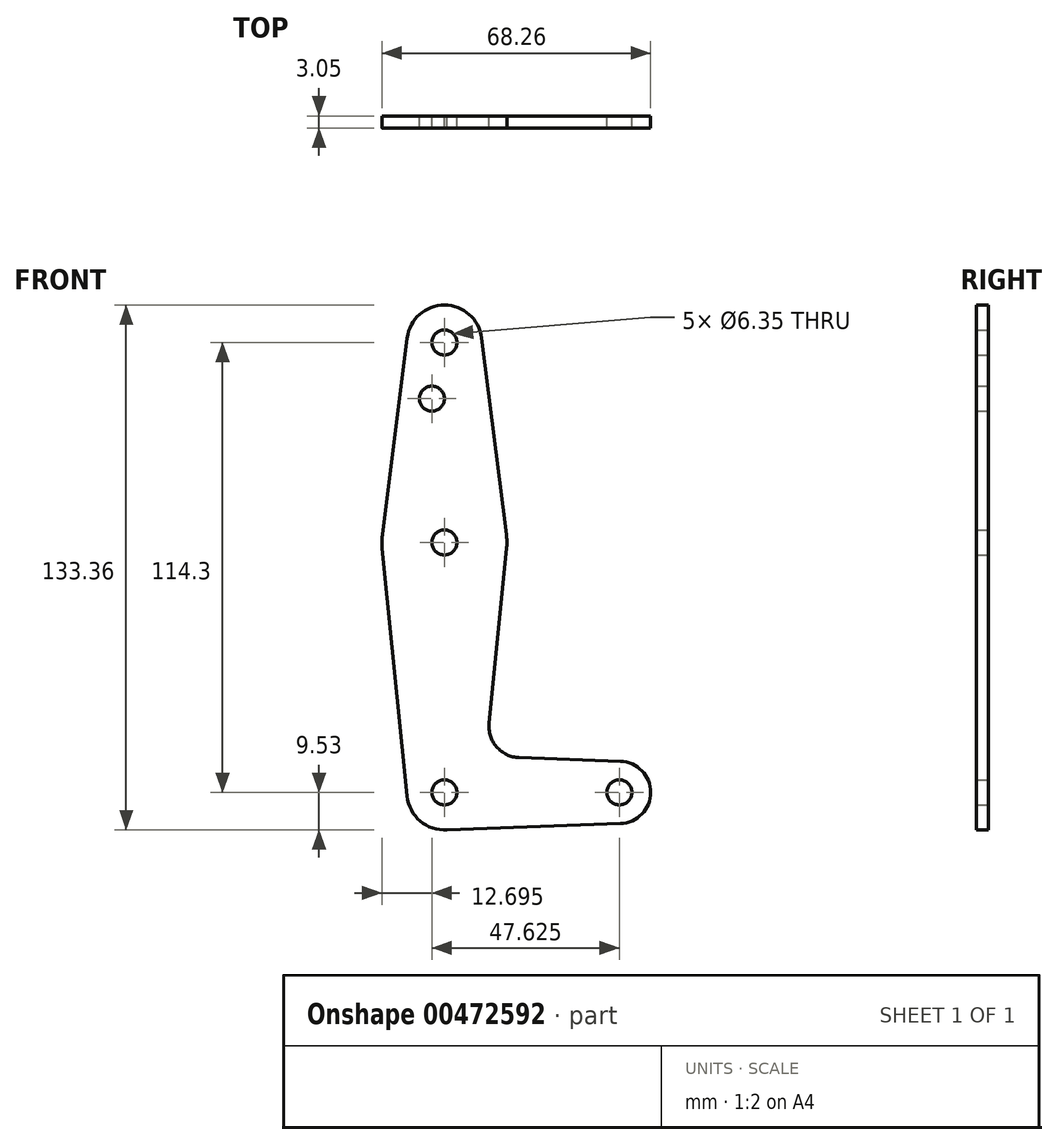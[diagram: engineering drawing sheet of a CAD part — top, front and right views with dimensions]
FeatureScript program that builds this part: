
annotation { "Feature Type Name" : "Feature", "Feature Type Description" : "" }
export const myFeature = defineFeature(function(context is Context, id is Id, definition is map)
    precondition{}
    {
        {
            var Q0;
            Q0=qCreatedBy(makeId("Front.planeOp"),FACE);
            var sketch = newSketch(context, id + "F0", { "sketchPlane" : qUnion([Q0])});
            skLineSegment(sketch, "E0", {"start": v(0, 0) * mm, "end": v(0, 114.3) * mm, "construction": true});
            skLineSegment(sketch, "E1", {"start": v(0, 0) * mm, "end": v(44.45, 0) * mm, "construction": true});
            skCircle(sketch, "E2", {"center": v(0, 114.3) * mm, "radius": 9.53 * mm});
            skLineSegment(sketch, "E3", {"start": v(0, 0) * mm, "end": v(0, 63.5) * mm, "construction": true});
            skCircle(sketch, "E4", {"center": v(0, 63.5) * mm, "radius": 15.88 * mm});
            skCircle(sketch, "E5", {"center": v(0, 0) * mm, "radius": 9.53 * mm});
            skCircle(sketch, "E6", {"center": v(44.45, 0) * mm, "radius": 7.94 * mm});
            skLineSegment(sketch, "E7", {"start": v(9.45, 115.5) * mm, "end": v(15.75, 65.48) * mm});
            skLineSegment(sketch, "E8", {"start": v(-15.8, 61.91) * mm, "end": v(-9.48, -0.95) * mm});
            skLineSegment(sketch, "E9", {"start": v(0, -9.53) * mm, "end": v(44.73, -7.93) * mm});
            skCircle(sketch, "E10", {"center": v(0, 114.3) * mm, "radius": 3.18 * mm});
            skCircle(sketch, "E11", {"center": v(0, 63.5) * mm, "radius": 3.18 * mm});
            skCircle(sketch, "E12", {"center": v(0, 0) * mm, "radius": 3.18 * mm});
            skCircle(sketch, "E13", {"center": v(-3.17, 100.03) * mm, "radius": 3.18 * mm});
            skLineSegment(sketch, "E14", {"start": v(-15.75, 65.48) * mm, "end": v(-9.45, 115.5) * mm});
            skCircle(sketch, "E15", {"center": v(44.45, 0) * mm, "radius": 3.18 * mm});
            skLineSegment(sketch, "E16", {"start": v(18.97, 8.85) * mm, "end": v(44.73, 7.93) * mm});
            skLineSegment(sketch, "E17", {"start": v(11.34, 17.59) * mm, "end": v(15.8, 61.91) * mm});
            skArc(sketch, "E18.filletArc", {"start": v(11.34, 17.59) * mm, "mid": v(13.26, 11.57) * mm, "end": v(18.97, 8.85) * mm});
            skSolve(sketch);
        }
        {
            var Q0;
            Q0 = qSketchRegion(id + "F0", true);
            extrude(context, id + "F1", {"entities" : qUnion([Q0]), "depth" : 3.05 * mm});
        }
    });
